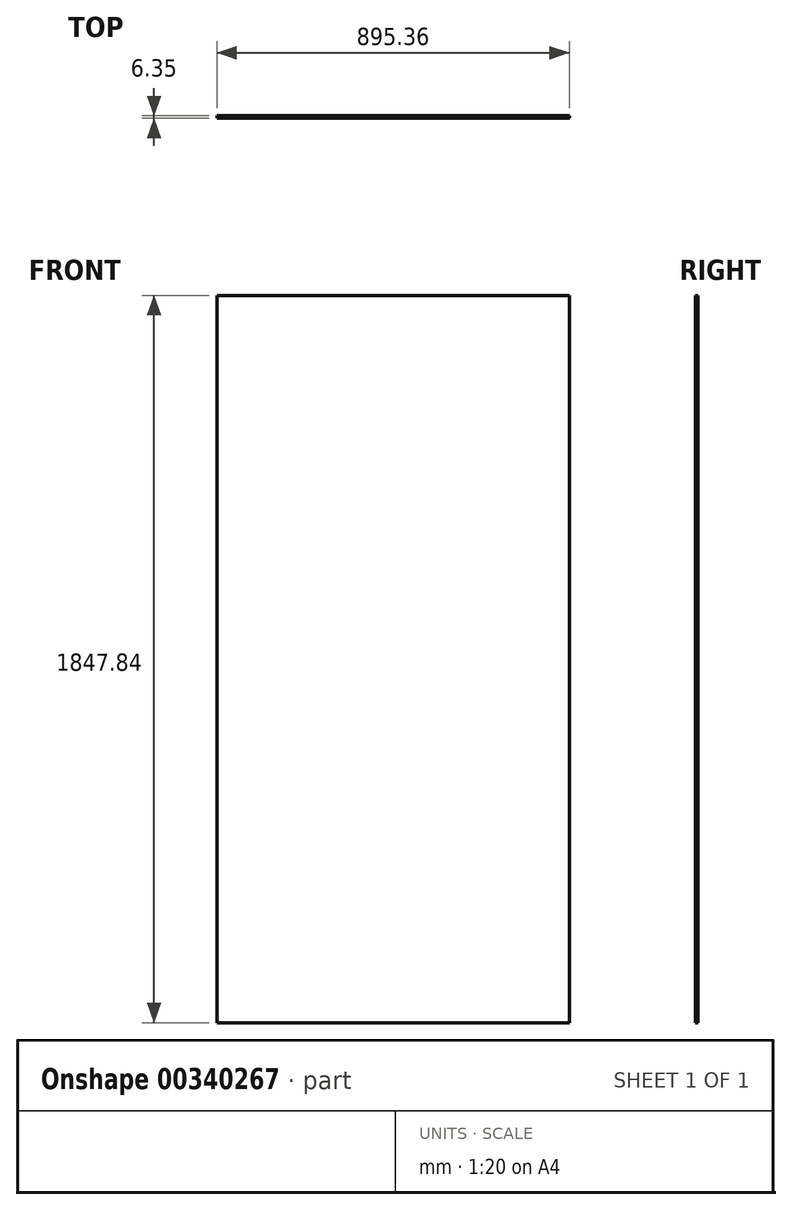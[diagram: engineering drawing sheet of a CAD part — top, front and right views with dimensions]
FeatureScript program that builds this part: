
annotation { "Feature Type Name" : "Feature", "Feature Type Description" : "" }
export const myFeature = defineFeature(function(context is Context, id is Id, definition is map)
    precondition{}
    {
        {
            var Q0;
            Q0=qCreatedBy(makeId("Front.planeOp"),FACE);
            var sketch = newSketch(context, id + "F0", { "sketchPlane" : qUnion([Q0])});
            skLineSegment(sketch, "E0.bottom", {"start": v(447.68, 923.93) * mm, "end": v(-447.67, 923.93) * mm});
            skLineSegment(sketch, "E0.top", {"start": v(447.67, -923.93) * mm, "end": v(-447.68, -923.93) * mm});
            skLineSegment(sketch, "E0.left", {"start": v(447.68, 923.93) * mm, "end": v(447.67, -923.93) * mm});
            skLineSegment(sketch, "E0.right", {"start": v(-447.67, 923.93) * mm, "end": v(-447.68, -923.93) * mm});
            skPoint(sketch, "E0.middle", {"position": v(0, 0) * mm});
            skSolve(sketch);
        }
        {
            var Q0;
            Q0 = qSketchRegion(id + "F0", true);
            extrude(context, id + "F1", {"entities" : qUnion([Q0]), "depth" : 6.35 * mm});
        }
    });
